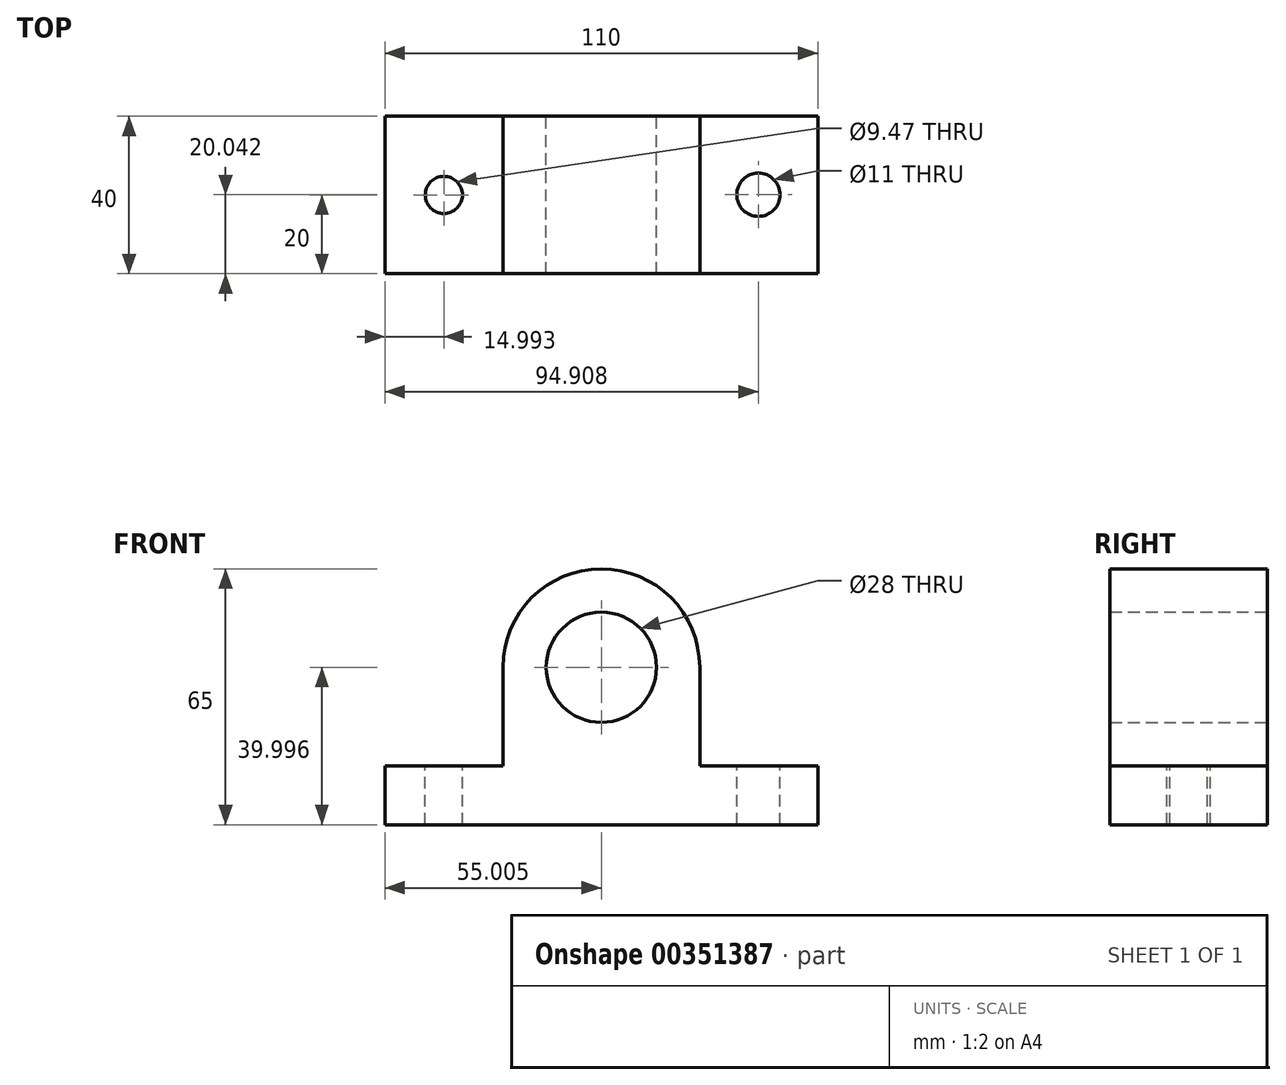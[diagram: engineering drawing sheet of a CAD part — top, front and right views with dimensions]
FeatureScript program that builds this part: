
annotation { "Feature Type Name" : "Feature", "Feature Type Description" : "" }
export const myFeature = defineFeature(function(context is Context, id is Id, definition is map)
    precondition{}
    {
        {
            var Q0;
            Q0=qCreatedBy(makeId("Front.planeOp"),FACE);
            var sketch = newSketch(context, id + "F0", { "sketchPlane" : qUnion([Q0])});
            skLineSegment(sketch, "E0", {"start": v(-43.8, -23.8) * mm, "end": v(66.2, -23.8) * mm});
            skLineSegment(sketch, "E1", {"start": v(66.2, -23.8) * mm, "end": v(66.2, -8.8) * mm});
            skLineSegment(sketch, "E2", {"start": v(66.2, -8.8) * mm, "end": v(36.2, -8.8) * mm});
            skLineSegment(sketch, "E3", {"start": v(36.2, 16.2) * mm, "end": v(36.2, -8.8) * mm});
            skLineSegment(sketch, "E4", {"start": v(-43.8, -23.8) * mm, "end": v(-43.8, -8.8) * mm});
            skLineSegment(sketch, "E5", {"start": v(-13.8, -8.8) * mm, "end": v(-43.8, -8.8) * mm});
            skLineSegment(sketch, "E6", {"start": v(-13.8, -8.8) * mm, "end": v(-13.8, 16.2) * mm});
            skPoint(sketch, "E7.startSnap0", {"position": v(-13.8, 3.7) * mm});
            skLineSegment(sketch, "E8", {"start": v(11.2, -23.8) * mm, "end": v(11.2, 24.6) * mm, "construction": true});
            skPoint(sketch, "E7.start.orphan", {"position": v(-13.8, -23.8) * mm});
            skLineSegment(sketch, "E9", {"start": v(-13.8, 16.2) * mm, "end": v(36.2, 16.2) * mm, "construction": true});
            skPoint(sketch, "E10.start.orphan", {"position": v(-50.18, -23.8) * mm});
            skArc(sketch, "E11", {"start": v(36.2, 16.2) * mm, "mid": v(11.2, 41.2) * mm, "end": v(-13.8, 16.2) * mm});
            skCircle(sketch, "E12", {"center": v(11.2, 16.2) * mm, "radius": 14 * mm});
            skSolve(sketch);
        }
        {
            var Q0;
            Q0 = qSketchRegion(id + "F0", true);
            extrude(context, id + "F1", {"entities" : qUnion([Q0]), "depth" : 40 * mm});
        }
        {
            var Q0;
            Q0=qCreatedBy(makeId("Top.planeOp"),FACE);
            var sketch = newSketch(context, id + "F2", { "sketchPlane" : qUnion([Q0])});
            skCircle(sketch, "E13", {"center": v(-28.82, -20) * mm, "radius": 4.73 * mm});
            skCircle(sketch, "E14", {"center": v(51.1, -19.96) * mm, "radius": 5.5 * mm});
            skPoint(sketch, "E15.start.orphan", {"position": v(-43.82, 0) * mm});
            skPoint(sketch, "E16.end.orphan", {"position": v(66.1, -19.96) * mm});
            skSolve(sketch);
        }
        {
            var Q0;
            Q0 = qSketchRegion(id + "F2", true);
            extrude(context, id + "F3", {"entities" : qUnion([Q0]), "operationType" : NewBodyOperationType.REMOVE, "oppositeDirection" : true, "depth" : 25 * mm});
        }
    });
